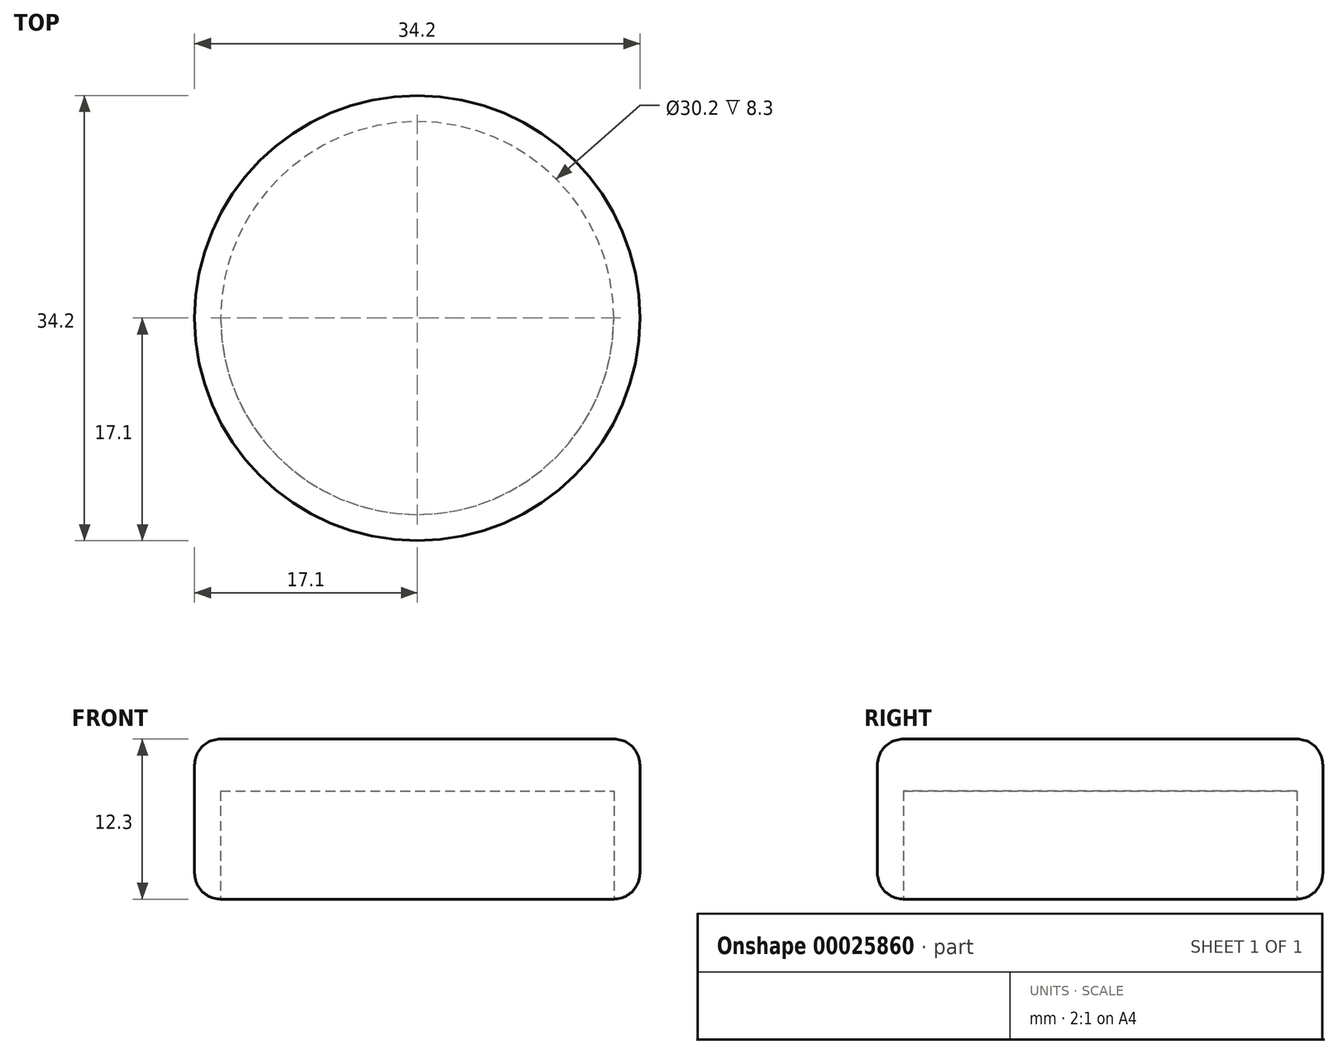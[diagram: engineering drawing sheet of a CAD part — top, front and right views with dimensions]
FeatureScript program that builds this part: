
annotation { "Feature Type Name" : "Feature", "Feature Type Description" : "" }
export const myFeature = defineFeature(function(context is Context, id is Id, definition is map)
    precondition{}
    {
        {
            var Q0;
            Q0=qCreatedBy(makeId("Top.planeOp"),FACE);
            var sketch = newSketch(context, id + "F0", { "sketchPlane" : qUnion([Q0])});
            skCircle(sketch, "E0", {"center": v(0, 0) * mm, "radius": 17.1 * mm});
            skSolve(sketch);
        }
        {
            var Q0;
            Q0 = qSketchRegion(id + "F0", true);
            extrude(context, id + "F1", {"entities" : qUnion([Q0]), "depth" : 12.3 * mm});
        }
        {
            var Q0;
            Q0=makeQuery(id+"F1.opExtrude","CAP_FACE",FACE,{"disambiguationData":[OSD([sQuery(id+"F0.wireOp",EDGE,"E0")])],"isStart":true});
            var sketch = newSketch(context, id + "F2", { "sketchPlane" : qUnion([Q0])});
            skCircle(sketch, "E1", {"center": v(0, 0) * mm, "radius": 15.1 * mm});
            skSolve(sketch);
        }
        {
            var Q0;
            Q0 = qSketchRegion(id + "F2", true);
            extrude(context, id + "F3", {"entities" : qUnion([Q0]), "operationType" : NewBodyOperationType.REMOVE, "oppositeDirection" : true, "depth" : 8.3 * mm});
        }
        {
            var Q0;
            Q0=makeQuery(id+"F1.opExtrude","CAP_EDGE",EDGE,{"disambiguationData":[OSD([sQuery(id+"F0.wireOp",EDGE,"E0")])],"isStart":false});
            fillet(context, id + "F4", {"entities" : qUnion([Q0]), "radius" : 2 * mm, "tangentPropagation" : true, "allowEdgeOverflow" : false});
        }
        {
            var Q0;
            Q0=makeQuery(id+"F1.opExtrude","CAP_EDGE",EDGE,{"disambiguationData":[OSD([sQuery(id+"F0.wireOp",EDGE,"E0")])],"isStart":true});
            fillet(context, id + "F5", {"entities" : qUnion([Q0]), "radius" : 2 * mm, "tangentPropagation" : true, "allowEdgeOverflow" : false});
        }
    });
